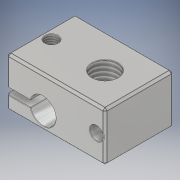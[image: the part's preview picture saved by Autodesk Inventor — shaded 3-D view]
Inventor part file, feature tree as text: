
AUTODESK INVENTOR PART (.ipt)
format: ipt  version: 2019 (Build 230136000, 136)  size: 389,632 bytes
history: native  units: mm
features: other x4, extrude x3, sketch x3, chamfer x1, fillet x1
ambient origin geometry x8: Origin, YZ Plane, XZ Plane, XY Plane, X Axis, Y Axis, Z Axis, Center Point
bodies: Solide1 (feature_tree)
feature tree (12):
  extrude  "Extrusion1"  Depth=23.0mm
  extrude  "Extrusion2"  Depth=11.5mm
  extrude  "Extrusion3"  Depth=14.5mm
  chamfer  "Chanfrein1"  Distance=1.5mm
  fillet  "Congé1"  Radius=2.0mm
  other  "Filetage1"
  other  "Filetage2"
  other  "Filetage3"
  other  "Filetage4"
  sketch  "Esquisse1"
  sketch  "Esquisse2"
  sketch  "Esquisse3"
